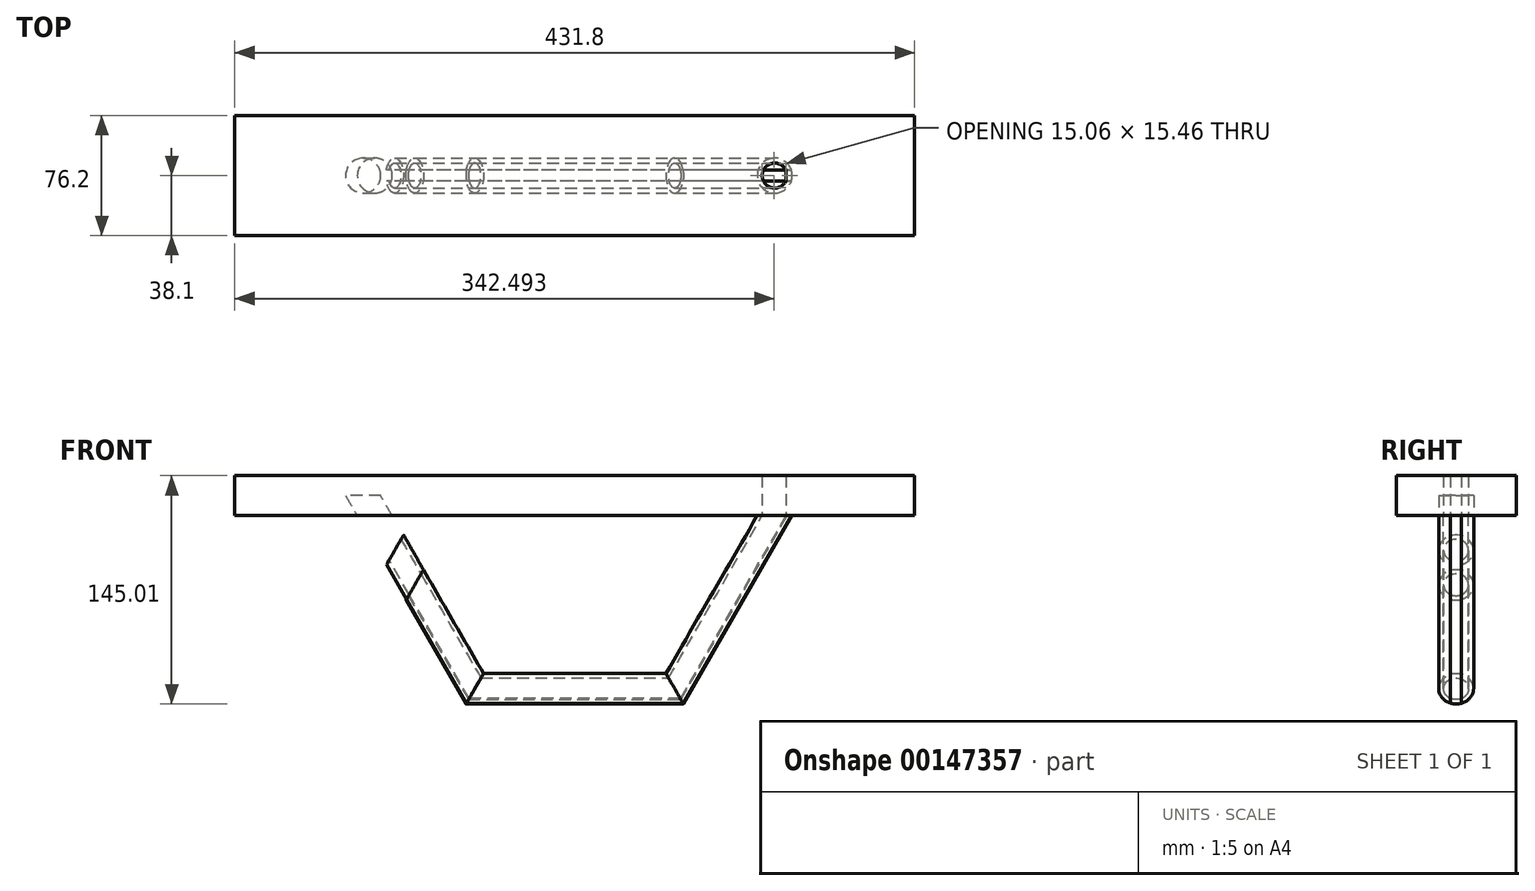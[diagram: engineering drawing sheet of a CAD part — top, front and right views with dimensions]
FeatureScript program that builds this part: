
annotation { "Feature Type Name" : "Feature", "Feature Type Description" : "" }
export const myFeature = defineFeature(function(context is Context, id is Id, definition is map)
    precondition{}
    {
        {
            var Q0;
            Q0=qCreatedBy(makeId("Top.planeOp"),FACE);
            var sketch = newSketch(context, id + "F0", { "sketchPlane" : qUnion([Q0])});
            skLineSegment(sketch, "E0.bottom", {"start": v(215.9, -38.1) * mm, "end": v(-215.9, -38.1) * mm});
            skLineSegment(sketch, "E0.top", {"start": v(215.9, 38.1) * mm, "end": v(-215.9, 38.1) * mm});
            skLineSegment(sketch, "E0.left", {"start": v(215.9, -38.1) * mm, "end": v(215.9, 38.1) * mm});
            skLineSegment(sketch, "E0.right", {"start": v(-215.9, -38.1) * mm, "end": v(-215.9, 38.1) * mm});
            skPoint(sketch, "E0.middle", {"position": v(0, 0) * mm});
            skCircle(sketch, "E1", {"center": v(-127, 0) * mm, "radius": 11.11 * mm});
            skCircle(sketch, "E2", {"center": v(127, 0) * mm, "radius": 11.11 * mm});
            skCircle(sketch, "E3", {"center": v(127, 0) * mm, "radius": 7.94 * mm});
            skLineSegment(sketch, "E4", {"start": v(127, 0) * mm, "end": v(145.04, 0) * mm, "construction": true});
            skLineSegment(sketch, "E5", {"start": v(134.12, -3.5) * mm, "end": v(134.12, 3.5) * mm});
            skLineSegment(sketch, "E6", {"start": v(138.11, -3.5) * mm, "end": v(138.11, 3.5) * mm});
            skLineSegment(sketch, "E7", {"start": v(134.12, -3.5) * mm, "end": v(138.11, -3.5) * mm});
            skLineSegment(sketch, "E8", {"start": v(134.12, 3.5) * mm, "end": v(138.11, 3.5) * mm});
            skSolve(sketch);
        }
        {
            var Q0;
            {var subQ0=sQuery(id+"F0.wireOp",EDGE,"E5");Q0=makeQuery(id+"F0.imprint","IMPRINT",FACE,{"disambiguationData":[TD([[makeQuery(id+"F0.imprint","IMPRINT",EDGE,{"derivedFrom":subQ0}),-1.0]])]});}
            var Q1;
            Q1=makeQuery(id+"F0.imprint","IMPRINT",FACE,{"disambiguationData":[TD([[makeQuery(id+"F0.imprint","IMPRINT",EDGE,{"derivedFrom":sQuery(id+"F0.wireOp",EDGE,"E0.bottom")}),-1.0]])]});
            var Q2;
            Q2=makeQuery(id+"F0.imprint","IMPRINT",FACE,{"disambiguationData":[TD([[makeQuery(id+"F0.imprint","IMPRINT",EDGE,{"derivedFrom":sQuery(id+"F0.wireOp",EDGE,"E1")}),1.0]])]});
            var Q3;
            {var subQ4=sQuery(id+"F0.wireOp",EDGE,"E2");var subQ6=sQuery(id+"F0.wireOp",EDGE,"E8");var subQ9=makeQuery(id+"F0.imprint","INTERSECT",VERTEX,{"derivedFrom":[subQ4,subQ6]});Q3=makeQuery(id+"F0.imprint","IMPRINT",FACE,{"disambiguationData":[TD([[makeQuery(id+"F0.imprint","IMPRINT",EDGE,{"disambiguationData":[TD([[subQ9,1.0]])],"derivedFrom":subQ4}),1.0]])]});}
            var Q4;
            {var subQ0=sQuery(id+"F0.wireOp",EDGE,"E8");var subQ1=sQuery(id+"F0.wireOp",EDGE,"E2");var subQ2=makeQuery(id+"F0.imprint","INTERSECT",VERTEX,{"derivedFrom":[subQ1,subQ0]});Q4=makeQuery(id+"F0.imprint","IMPRINT",FACE,{"disambiguationData":[TD([[makeQuery(id+"F0.imprint","IMPRINT",EDGE,{"disambiguationData":[TD([[subQ2,-1.0]])],"derivedFrom":subQ1}),1.0]])]});}
            var Q5;
            {var subQ0=sQuery(id+"F0.wireOp",EDGE,"E6");var subQ1=sQuery(id+"F0.wireOp",EDGE,"E2");var subQ2=makeQuery(id+"F0.imprint","INTERSECT",VERTEX,{"derivedFrom":[subQ1,subQ0]});Q5=makeQuery(id+"F0.imprint","IMPRINT",FACE,{"disambiguationData":[TD([[makeQuery(id+"F0.imprint","IMPRINT",EDGE,{"disambiguationData":[TD([[subQ2,1.0]])],"derivedFrom":subQ1}),-1.0]])]});}
            var Q6;
            {var subQ0=sQuery(id+"F0.wireOp",EDGE,"E8");var subQ1=sQuery(id+"F0.wireOp",EDGE,"E2");var subQ2=makeQuery(id+"F0.imprint","INTERSECT",VERTEX,{"derivedFrom":[subQ1,subQ0]});Q6=makeQuery(id+"F0.imprint","IMPRINT",FACE,{"disambiguationData":[TD([[makeQuery(id+"F0.imprint","IMPRINT",EDGE,{"disambiguationData":[TD([[subQ2,1.0]])],"derivedFrom":subQ1}),-1.0]])]});}
            var Q7;
            Q7 = qSketchRegion(id + "F2", true);
            extrude(context, id + "F1", {"entities" : qUnion([Q0, Q1, Q2, Q3, Q4, Q5, Q6, Q7]), "depth" : 25.4 * mm});
        }
        {
            var Q0;
            Q0=qCreatedBy(makeId("Front.planeOp"),FACE);
            var sketch = newSketch(context, id + "F2", { "sketchPlane" : qUnion([Q0])});
            skLineSegment(sketch, "E9", {"start": v(-63.5, -109.99) * mm, "end": v(63.5, -109.99) * mm});
            skLineSegment(sketch, "E10", {"start": v(63.5, -109.99) * mm, "end": v(127, 0) * mm});
            skLineSegment(sketch, "E11", {"start": v(127, 0) * mm, "end": v(134.33, 12.7) * mm});
            skLineSegment(sketch, "E12", {"start": v(-127, 0) * mm, "end": v(-134.33, 12.7) * mm});
            skLineSegment(sketch, "E13", {"start": v(-127, 0) * mm, "end": v(-114.3, -22) * mm});
            skLineSegment(sketch, "E14", {"start": v(-114.3, -22) * mm, "end": v(-101.6, -44) * mm});
            skLineSegment(sketch, "E15", {"start": v(-101.6, -44) * mm, "end": v(-63.5, -109.99) * mm});
            skSolve(sketch);
        }
        {
            var Q0;
            {var subQ4=sQuery(id+"F0.wireOp",EDGE,"E2");var subQ6=sQuery(id+"F0.wireOp",EDGE,"E8");var subQ9=makeQuery(id+"F0.imprint","INTERSECT",VERTEX,{"derivedFrom":[subQ4,subQ6]});Q0=makeQuery(id+"F0.imprint","IMPRINT",FACE,{"disambiguationData":[TD([[makeQuery(id+"F0.imprint","IMPRINT",EDGE,{"disambiguationData":[TD([[subQ9,1.0]])],"derivedFrom":subQ4}),1.0]])]});}
            var Q1;
            Q1=sQuery(id+"F2.wireOp",EDGE,"E10");
            var Q2;
            Q2=sQuery(id+"F2.wireOp",EDGE,"E9");
            var Q3;
            Q3=sQuery(id+"F2.wireOp",EDGE,"E15");
            sweep(context, id + "F3", {"profiles" : qUnion([Q0]), "path" : qUnion([Q1, Q2, Q3])});
        }
        {
            var Q0;
            {var subQ0=sQuery(id+"F0.wireOp",EDGE,"E8");var subQ1=sQuery(id+"F0.wireOp",EDGE,"E2");var subQ2=makeQuery(id+"F0.imprint","INTERSECT",VERTEX,{"derivedFrom":[subQ1,subQ0]});Q0=makeQuery(id+"F0.imprint","IMPRINT",FACE,{"disambiguationData":[TD([[makeQuery(id+"F0.imprint","IMPRINT",EDGE,{"disambiguationData":[TD([[subQ2,-1.0]])],"derivedFrom":subQ1}),1.0]])]});}
            var Q1;
            Q1=sQuery(id+"F2.wireOp",EDGE,"E15");
            var Q2;
            Q2=sQuery(id+"F2.wireOp",EDGE,"E9");
            var Q3;
            Q3=sQuery(id+"F2.wireOp",EDGE,"E10");
            var Q4;
            Q4=sQuery(id+"F2.wireOp",EDGE,"E14");
            sweep(context, id + "F4", {"profiles" : qUnion([Q0]), "path" : qUnion([Q1, Q2, Q3, Q4])});
        }
        {
            var Q0;
            Q0=makeQuery(id+"F0.imprint","IMPRINT",FACE,{"disambiguationData":[TD([[makeQuery(id+"F0.imprint","IMPRINT",EDGE,{"derivedFrom":sQuery(id+"F0.wireOp",EDGE,"E1")}),1.0]])]});
            var Q1;
            Q1=sQuery(id+"F2.wireOp",EDGE,"E12");
            sweep(context, id + "F5", {"operationType" : NewBodyOperationType.REMOVE, "profiles" : qUnion([Q0]), "path" : qUnion([Q1])});
        }
    });
